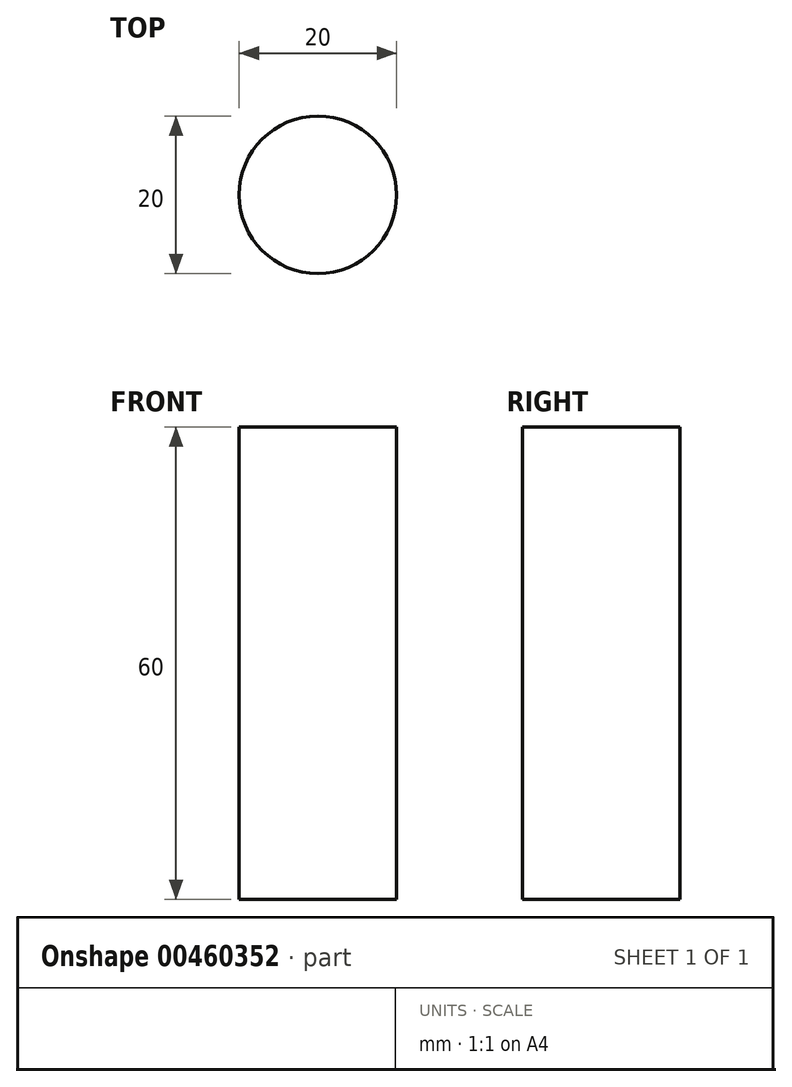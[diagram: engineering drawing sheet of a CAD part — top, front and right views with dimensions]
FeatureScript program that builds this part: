
annotation { "Feature Type Name" : "Feature", "Feature Type Description" : "" }
export const myFeature = defineFeature(function(context is Context, id is Id, definition is map)
    precondition{}
    {
        {
            var Q0;
            Q0=qCreatedBy(makeId("Top.planeOp"),FACE);
            var sketch = newSketch(context, id + "F0", { "sketchPlane" : qUnion([Q0])});
            skCircle(sketch, "E0", {"center": v(0, 0) * mm, "radius": 10 * mm});
            skSolve(sketch);
        }
        {
            var Q0;
            Q0=makeQuery(id+"F0.imprint","IMPRINT",FACE,{"disambiguationData":[TD([[makeQuery(id+"F0.imprint","IMPRINT",EDGE,{"derivedFrom":sQuery(id+"F0.wireOp",EDGE,"E0")}),1.0]])]});
            extrude(context, id + "F1", {"entities" : qUnion([Q0]), "depth" : 60 * mm});
        }
    });
